annotation { "Feature Type Name" : "Feature", "Feature Type Description" : "" }
export const myFeature = defineFeature(function(context is Context, id is Id, definition is map)
    precondition{}
    {
        {
            var Q0;
            Q0=qCreatedBy(makeId("Top.planeOp"),FACE);
            var sketch = newSketch(context, id + "F0", { "sketchPlane" : qUnion([Q0])});
            skLineSegment(sketch, "E0.bottom", {"start": v(0, 0) * mm, "end": v(63.5, 0) * mm});
            skLineSegment(sketch, "E0.top", {"start": v(0, 19.05) * mm, "end": v(63.5, 19.05) * mm});
            skLineSegment(sketch, "E0.left", {"start": v(0, 0) * mm, "end": v(0, 19.05) * mm});
            skLineSegment(sketch, "E0.right", {"start": v(63.5, 0) * mm, "end": v(63.5, 19.05) * mm});
            skSolve(sketch);
        }
        {
            var Q0;
            Q0=makeQuery(id+"F0.imprint","IMPRINT",FACE,{"disambiguationData":[TD([[makeQuery(id+"F0.imprint","IMPRINT",EDGE,{"derivedFrom":sQuery(id+"F0.wireOp",EDGE,"E0.bottom")}),1.0]])]});
            extrude(context, id + "F1", {"entities" : qUnion([Q0]), "depth" : 3.8 * mm, "offsetDistance" : 25.4 * mm});
        }
        {
            var Q0;
            Q0=makeQuery(id+"F1.opExtrude","CAP_FACE",FACE,{"disambiguationData":[OSD([sQuery(id+"F0.wireOp",EDGE,"E0.bottom"),sQuery(id+"F0.wireOp",EDGE,"E0.top"),sQuery(id+"F0.wireOp",EDGE,"E0.left"),sQuery(id+"F0.wireOp",EDGE,"E0.right")])],"isStart":false});
            var sketch = newSketch(context, id + "F2", { "sketchPlane" : qUnion([Q0])});
            skLineSegment(sketch, "E1", {"start": v(17.63, 12.35) * mm, "end": v(17.63, 8.25) * mm});
            skLineSegment(sketch, "E2", {"start": v(19.96, 8.25) * mm, "end": v(20.18, 9.36) * mm});
            skLineSegment(sketch, "E3", {"start": v(20.18, 9.36) * mm, "end": v(20.79, 9.36) * mm});
            skLineSegment(sketch, "E4", {"start": v(17.63, 12.35) * mm, "end": v(32.8, 12.35) * mm});
            skLineSegment(sketch, "E5", {"start": v(32.8, 12.35) * mm, "end": v(32.8, 8.24) * mm});
            skLineSegment(sketch, "E6", {"start": v(32.8, 8.24) * mm, "end": v(30.46, 8.24) * mm});
            skLineSegment(sketch, "E7", {"start": v(30.46, 8.24) * mm, "end": v(30.24, 9.4) * mm});
            skLineSegment(sketch, "E8", {"start": v(30.24, 9.4) * mm, "end": v(27.41, 9.4) * mm});
            skLineSegment(sketch, "E9", {"start": v(27.41, 9.4) * mm, "end": v(27.41, 4.4) * mm});
            skLineSegment(sketch, "E10", {"start": v(27.41, 4.4) * mm, "end": v(28.8, 4.4) * mm});
            skLineSegment(sketch, "E11", {"start": v(28.8, 4.4) * mm, "end": v(28.8, 1.72) * mm});
            skLineSegment(sketch, "E12", {"start": v(28.8, 1.72) * mm, "end": v(22.5, 1.72) * mm});
            skLineSegment(sketch, "E13", {"start": v(22.5, 1.72) * mm, "end": v(22.5, 4.34) * mm});
            skLineSegment(sketch, "E14", {"start": v(22.5, 4.34) * mm, "end": v(23.97, 4.34) * mm});
            skLineSegment(sketch, "E15", {"start": v(23.97, 4.34) * mm, "end": v(23.97, 9.4) * mm});
            skLineSegment(sketch, "E16", {"start": v(23.97, 9.4) * mm, "end": v(23.18, 9.4) * mm});
            skLineSegment(sketch, "E17", {"start": v(23.18, 9.4) * mm, "end": v(23.18, 4.89) * mm});
            skLineSegment(sketch, "E18", {"start": v(23.18, 4.89) * mm, "end": v(20.45, 4.89) * mm});
            skLineSegment(sketch, "E19", {"start": v(20.45, 4.89) * mm, "end": v(20.45, 5.16) * mm});
            skLineSegment(sketch, "E20", {"start": v(20.5, 12.75) * mm, "end": v(23, 12.75) * mm});
            skLineSegment(sketch, "E21", {"start": v(23, 12.75) * mm, "end": v(23, 17.28) * mm});
            skLineSegment(sketch, "E22", {"start": v(23, 17.28) * mm, "end": v(20.4, 17.28) * mm});
            skLineSegment(sketch, "E23", {"start": v(20.4, 17.28) * mm, "end": v(20.4, 15.97) * mm});
            skArc(sketch, "E24", {"start": v(20.5, 12.75) * mm, "mid": v(18.85, 13.8) * mm, "end": v(16.94, 14.27) * mm});
            skArc(sketch, "E25", {"start": v(16.94, 14.27) * mm, "mid": v(15.06, 14.13) * mm, "end": v(13.4, 13.22) * mm});
            skArc(sketch, "E26", {"start": v(13.4, 13.22) * mm, "mid": v(12.16, 11.86) * mm, "end": v(11.93, 10.03) * mm});
            skArc(sketch, "E27", {"start": v(11.93, 10.03) * mm, "mid": v(12.33, 8.67) * mm, "end": v(13.4, 7.75) * mm});
            skArc(sketch, "E28", {"start": v(13.4, 7.75) * mm, "mid": v(14.57, 7.03) * mm, "end": v(15.89, 6.7) * mm});
            skArc(sketch, "E29", {"start": v(15.89, 6.7) * mm, "mid": v(17.26, 6.72) * mm, "end": v(18.59, 7.08) * mm});
            skArc(sketch, "E30", {"start": v(18.59, 7.08) * mm, "mid": v(19.7, 7.67) * mm, "end": v(20.5, 8.63) * mm});
            skArc(sketch, "E31", {"start": v(20.5, 8.63) * mm, "mid": v(20.65, 8.99) * mm, "end": v(20.79, 9.36) * mm});
            skArc(sketch, "E32", {"start": v(18.42, 4.48) * mm, "mid": v(19.45, 4.8) * mm, "end": v(20.45, 5.16) * mm});
            skArc(sketch, "E33", {"start": v(14.5, 4.03) * mm, "mid": v(16.48, 4.1) * mm, "end": v(18.42, 4.48) * mm});
            skArc(sketch, "E34", {"start": v(11.06, 5.16) * mm, "mid": v(12.73, 4.45) * mm, "end": v(14.5, 4.03) * mm});
            skArc(sketch, "E35", {"start": v(9.43, 6.45) * mm, "mid": v(10.23, 5.79) * mm, "end": v(11.06, 5.16) * mm});
            skArc(sketch, "E36", {"start": v(8.17, 8.63) * mm, "mid": v(8.69, 7.47) * mm, "end": v(9.43, 6.45) * mm});
            skArc(sketch, "E37", {"start": v(7.83, 10.88) * mm, "mid": v(7.8, 9.72) * mm, "end": v(8.17, 8.63) * mm});
            skArc(sketch, "E38", {"start": v(8.51, 13.22) * mm, "mid": v(8.07, 12.08) * mm, "end": v(7.83, 10.88) * mm});
            skArc(sketch, "E39", {"start": v(9.93, 14.94) * mm, "mid": v(9.16, 14.13) * mm, "end": v(8.51, 13.22) * mm});
            skArc(sketch, "E40", {"start": v(11.93, 16.26) * mm, "mid": v(10.88, 15.67) * mm, "end": v(9.93, 14.94) * mm});
            skArc(sketch, "E41", {"start": v(14.05, 17.07) * mm, "mid": v(12.96, 16.74) * mm, "end": v(11.93, 16.26) * mm});
            skArc(sketch, "E42", {"start": v(17.15, 17.07) * mm, "mid": v(15.6, 17.21) * mm, "end": v(14.05, 17.07) * mm});
            skArc(sketch, "E43", {"start": v(20.4, 15.97) * mm, "mid": v(18.84, 16.71) * mm, "end": v(17.15, 17.07) * mm});
            skLineSegment(sketch, "E44", {"start": v(17.63, 8.25) * mm, "end": v(19.96, 8.25) * mm});
            skSolve(sketch);
        }
        {
            var Q0;
            Q0 = qSketchRegion(id + "F2", true);
            var Q1;
            Q1=makeQuery(id+"F2.imprint","IMPRINT",FACE,{"disambiguationData":[TD([[makeQuery(id+"F2.imprint","IMPRINT",EDGE,{"derivedFrom":sQuery(id+"F2.wireOp",EDGE,"E1")}),1.0]])]});
            extrude(context, id + "F3", {"entities" : qUnion([Q0, Q1]), "operationType" : NewBodyOperationType.REMOVE, "oppositeDirection" : true, "depth" : 1.27 * mm, "offsetDistance" : 25.4 * mm});
        }
        {
            var Q0;
            Q0=makeQuery(id+"F1.opExtrude","SWEPT_EDGE",EDGE,{"disambiguationData":[OSD([sQuery(id+"F0.wireOp",EDGE,"E0.bottom"),sQuery(id+"F0.wireOp",EDGE,"E0.left")])]});
            fillet(context, id + "F4", {"entities" : qUnion([Q0]), "radius" : 7.62 * mm, "tangentPropagation" : true, "allowEdgeOverflow" : false});
        }
        {
            var Q0;
            Q0=makeQuery(id+"F1.opExtrude","SWEPT_EDGE",EDGE,{"disambiguationData":[OSD([sQuery(id+"F0.wireOp",EDGE,"E0.top"),sQuery(id+"F0.wireOp",EDGE,"E0.left")])]});
            fillet(context, id + "F5", {"entities" : qUnion([Q0]), "radius" : 7.62 * mm, "tangentPropagation" : true, "allowEdgeOverflow" : false});
        }
        {
            var Q0;
            Q0=makeQuery(id+"F1.opExtrude","SWEPT_EDGE",EDGE,{"disambiguationData":[OSD([sQuery(id+"F0.wireOp",EDGE,"E0.bottom"),sQuery(id+"F0.wireOp",EDGE,"E0.right")])]});
            chamfer(context, id + "F6", {"entities" : qUnion([Q0]), "width" : 5.08 * mm, "tangentPropagation" : true});
        }
        {
            var Q0;
            Q0=makeQuery(id+"F1.opExtrude","SWEPT_EDGE",EDGE,{"disambiguationData":[OSD([sQuery(id+"F0.wireOp",EDGE,"E0.top"),sQuery(id+"F0.wireOp",EDGE,"E0.right")])]});
            chamfer(context, id + "F7", {"entities" : qUnion([Q0]), "width" : 5.08 * mm, "tangentPropagation" : true});
        }
        {
            var Q0;
            Q0=makeQuery(id+"F1.opExtrude","CAP_FACE",FACE,{"disambiguationData":[OSD([sQuery(id+"F0.wireOp",EDGE,"E0.bottom"),sQuery(id+"F0.wireOp",EDGE,"E0.top"),sQuery(id+"F0.wireOp",EDGE,"E0.left"),sQuery(id+"F0.wireOp",EDGE,"E0.right")])],"isStart":false});
            var sketch = newSketch(context, id + "F8", { "sketchPlane" : qUnion([Q0])});
            skText(sketch, "E45", { "text": "Aleksander Lucy\nGTRI ATAS Intern\n(470) 209 - 4806", "fontName": "OpenSans-Regular.ttf"});
            const initialGuessF8  = {"E45": [0.03732, 0.01212, 1, 0, 0.00203]};
            skSetInitialGuess(sketch, initialGuessF8);
            skSolve(sketch);
        }
        {
            var Q0;
            Q0 = qSketchRegion(id + "F8", true);
            extrude(context, id + "F9", {"entities" : qUnion([Q0]), "operationType" : NewBodyOperationType.REMOVE, "oppositeDirection" : true, "depth" : 1.27 * mm, "offsetDistance" : 25.4 * mm});
        }
        {
            var Q0;
            {var subQ0=sQuery(id+"F0.wireOp",EDGE,"E0.left");var subQ1=sQuery(id+"F0.wireOp",EDGE,"E0.top");var subQ2=sQuery(id+"F0.wireOp",EDGE,"E0.bottom");var subQ3=sQuery(id+"F0.wireOp",EDGE,"E0.right");Q0=makeQuery(id+"F9.boolean.opBoolean","SPLIT",FACE,{"disambiguationData":[TD([makeQuery(id+"F1.opExtrude","SWEPT_FACE",FACE,{"disambiguationData":[OSD([subQ2])]})])],"derivedFrom":makeQuery(id+"F1.opExtrude","CAP_FACE",FACE,{"disambiguationData":[OSD([subQ2,subQ1,subQ0,subQ3])],"isStart":false})});}
            var sketch = newSketch(context, id + "F10", { "sketchPlane" : qUnion([Q0])});
            skLineSegment(sketch, "E46.bottom", {"start": v(0, 11.43) * mm, "end": v(-3.81, 11.43) * mm});
            skLineSegment(sketch, "E46.top", {"start": v(0, 7.62) * mm, "end": v(-3.81, 7.62) * mm});
            skLineSegment(sketch, "E46.left", {"start": v(0, 11.43) * mm, "end": v(0, 7.62) * mm});
            skLineSegment(sketch, "E46.right", {"start": v(-3.81, 11.43) * mm, "end": v(-3.8, 7.62) * mm});
            skCircle(sketch, "E47", {"center": v(-1.9, 9.53) * mm, "radius": 1.27 * mm});
            skSolve(sketch);
        }
        {
            var Q0;
            Q0 = qSketchRegion(id + "F10", true);
            var Q1;
            Q1=makeQuery(id+"F10.imprint","IMPRINT",FACE,{"disambiguationData":[TD([[makeQuery(id+"F10.imprint","IMPRINT",EDGE,{"derivedFrom":sQuery(id+"F10.wireOp",EDGE,"E46.bottom")}),1.0]])]});
            extrude(context, id + "F11", {"entities" : qUnion([Q0, Q1]), "operationType" : NewBodyOperationType.ADD, "depth" : -3.8 * mm, "offsetDistance" : 25.4 * mm});
        }
    });